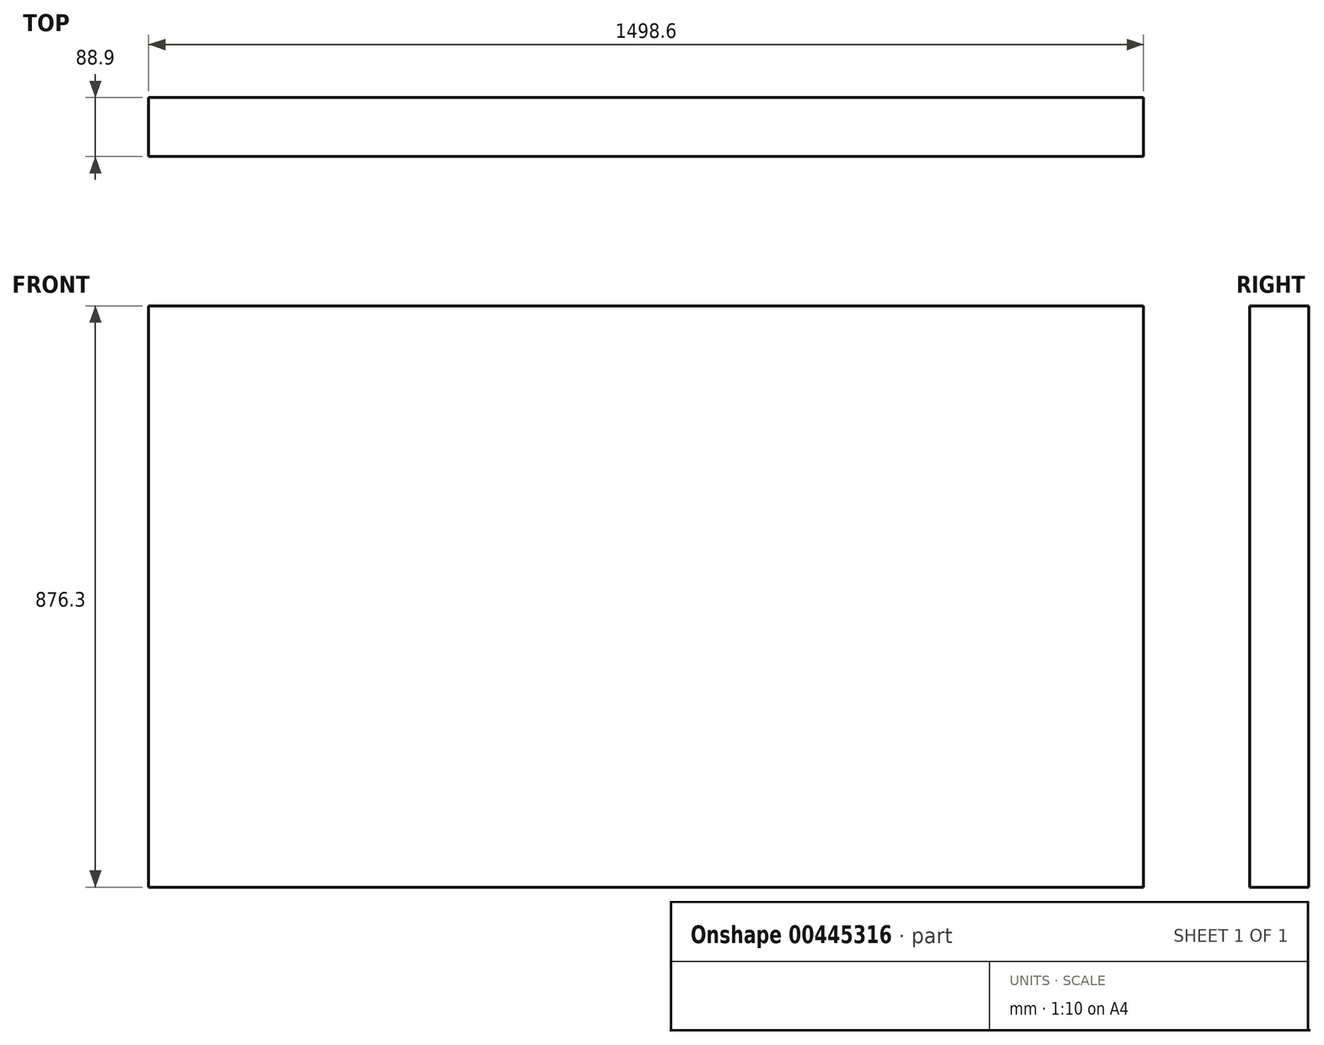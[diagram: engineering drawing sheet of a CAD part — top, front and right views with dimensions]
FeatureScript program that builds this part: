
annotation { "Feature Type Name" : "Feature", "Feature Type Description" : "" }
export const myFeature = defineFeature(function(context is Context, id is Id, definition is map)
    precondition{}
    {
        {
            var Q0;
            Q0=qCreatedBy(makeId("Front.planeOp"),FACE);
            var sketch = newSketch(context, id + "F0", { "sketchPlane" : qUnion([Q0])});
            skLineSegment(sketch, "E0.bottom", {"start": v(-81.6, 0) * mm, "end": v(1417, 0) * mm});
            skLineSegment(sketch, "E0.top", {"start": v(-81.6, 876.3) * mm, "end": v(1417, 876.3) * mm});
            skLineSegment(sketch, "E0.left", {"start": v(-81.6, 0) * mm, "end": v(-81.6, 876.3) * mm});
            skLineSegment(sketch, "E0.right", {"start": v(1417, 0) * mm, "end": v(1417, 876.3) * mm});
            skSolve(sketch);
        }
        {
            var Q0;
            Q0=makeQuery(id+"F0.imprint","IMPRINT",FACE,{"disambiguationData":[TD([[makeQuery(id+"F0.imprint","IMPRINT",EDGE,{"derivedFrom":sQuery(id+"F0.wireOp",EDGE,"E0.bottom")}),1.0]])]});
            extrude(context, id + "F1", {"entities" : qUnion([Q0]), "depth" : 88.9 * mm});
        }
    });
